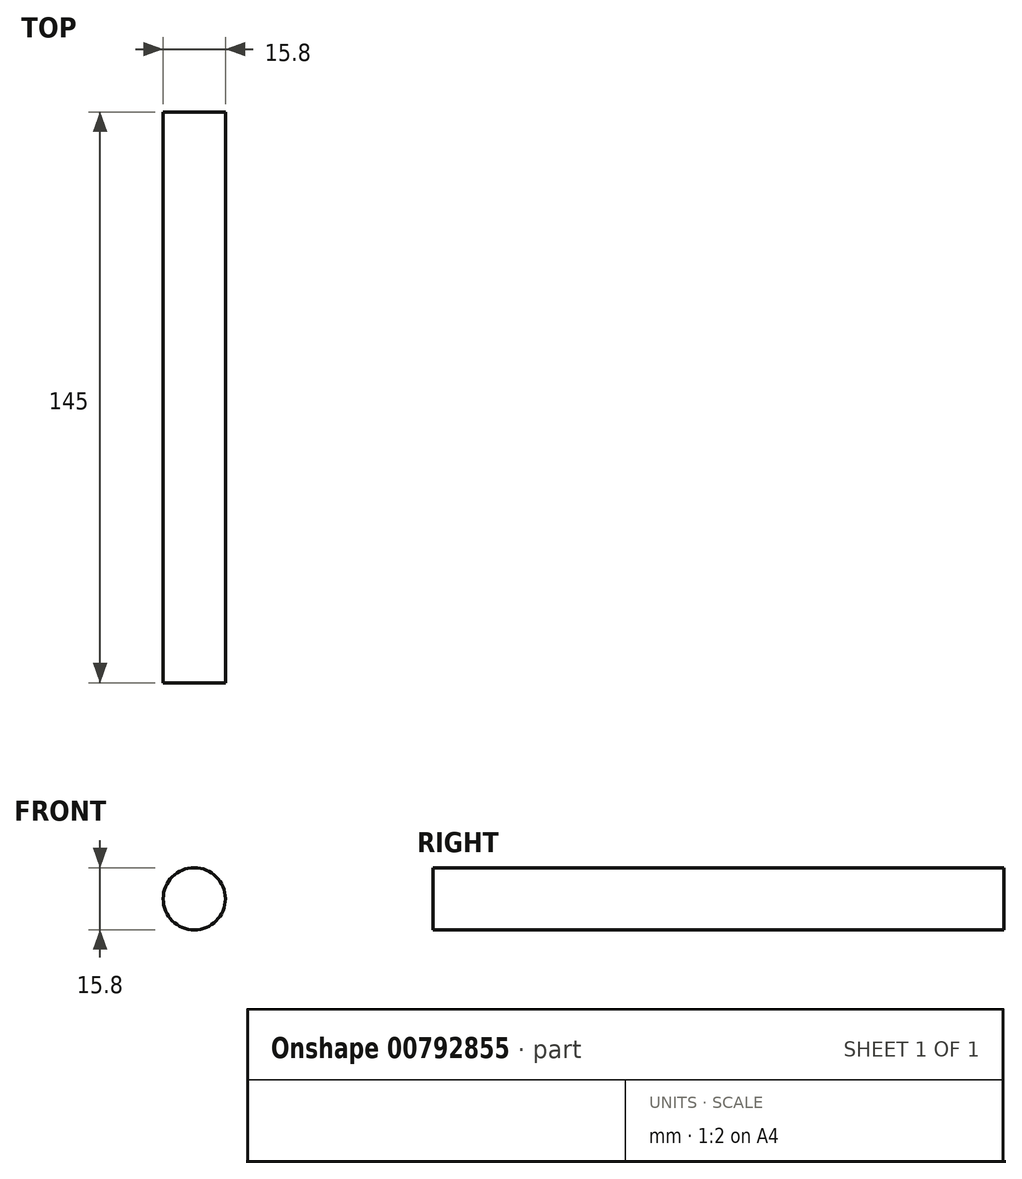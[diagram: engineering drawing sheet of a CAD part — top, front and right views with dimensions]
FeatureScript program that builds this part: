
annotation { "Feature Type Name" : "Feature", "Feature Type Description" : "" }
export const myFeature = defineFeature(function(context is Context, id is Id, definition is map)
    precondition{}
    {
        {
            var Q0;
            Q0=qCreatedBy(makeId("Front.planeOp"),FACE);
            var sketch = newSketch(context, id + "F0", { "sketchPlane" : qUnion([Q0])});
            skCircle(sketch, "E0", {"center": v(0, 0) * mm, "radius": 7.9 * mm});
            skSolve(sketch);
        }
        {
            var Q0;
            Q0 = qSketchRegion(id + "F0", true);
            extrude(context, id + "F1", {"entities" : qUnion([Q0]), "depth" : 145 * mm, "offsetDistance" : 25 * mm});
        }
    });
